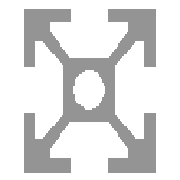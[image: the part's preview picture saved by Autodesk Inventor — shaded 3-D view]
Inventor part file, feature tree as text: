
AUTODESK INVENTOR PART (.ipt)
format: ipt  version: 2024 (Build 280153000, 153)  size: 228,352 bytes
history: native  units: in
note: dims shown in document units (in); Inventor stores cm internally (conversion verified against a paired STEP export)
features: other x26, extrude x1, fillet x1
ambient origin geometry x8: Origin, YZ Plane, XZ Plane, XY Plane, X Axis, Y Axis, Z Axis, Center Point
bodies: Body1 (feature_tree)
feature tree (28):
  other  "Table"
  other  "20x20 Channel-10"
  other  "20x20 Channel-20"
  other  "20x20 Channel-30"
  other  "20x20 Channel-40"
  other  "20x20 Channel-50"
  other  "20x20 Channel-100"
  other  "20x20 Channel-150"
  other  "20x20 Channel-200"
  other  "20x20 Channel-250"
  other  "20x20 Channel-300"
  other  "20x20 Channel-350"
  other  "20x20 Channel-400"
  other  "20x20 Channel-450"
  other  "20x20 Channel-500"
  other  "20x20 Channel-550"
  other  "20x20 Channel-560"
  other  "20x20 Channel-570"
  other  "20x20 Channel-580"
  other  "20x20 Channel-590"
  other  "20x20 Channel-600"
  other  "20x20 Channel-610"
  other  "20x20 Channel-620"
  other  "20x20 Channel-630"
  other  "20x20 Channel-640"
  other  "20x20 Channel-650"
  extrude  "Extrusion3"  Depth=0.7874in
  fillet  "Fillet2"  Radius=0.7874in
